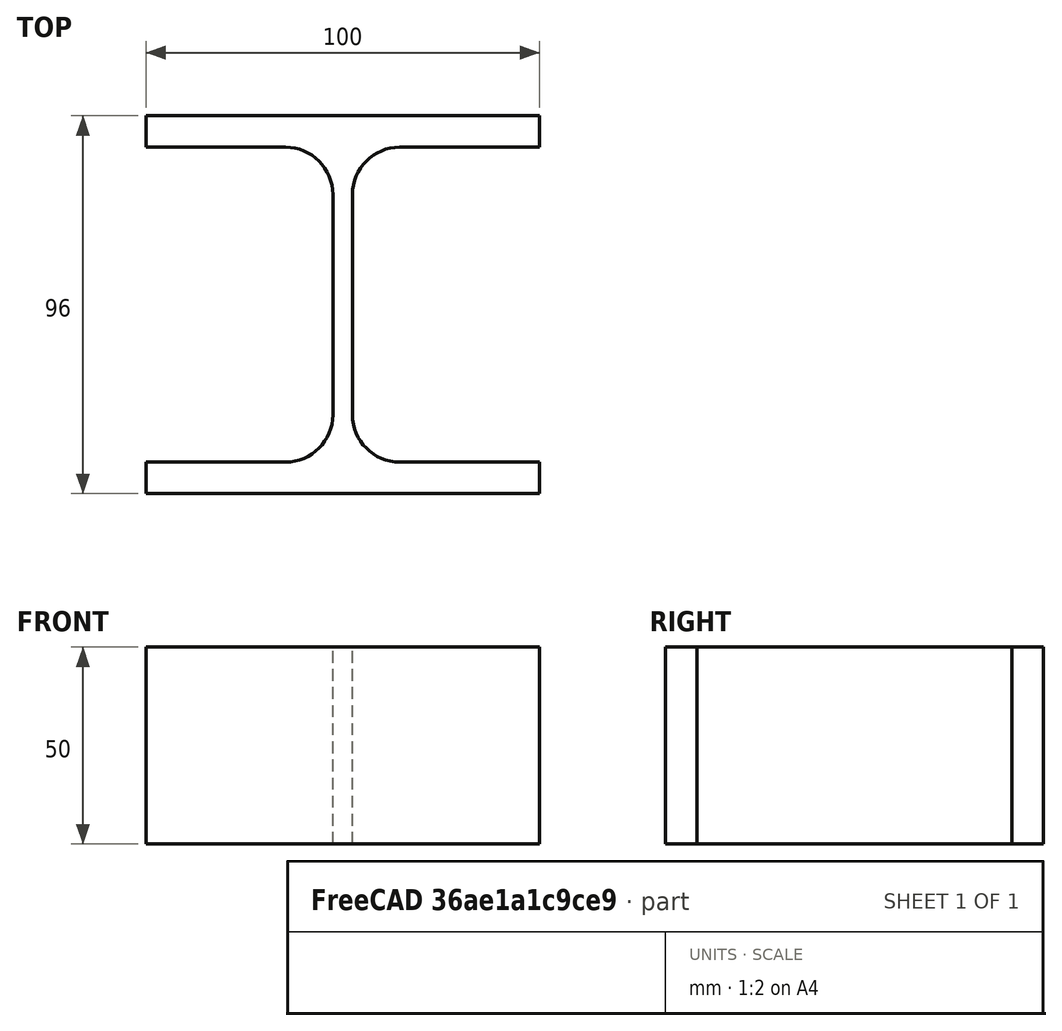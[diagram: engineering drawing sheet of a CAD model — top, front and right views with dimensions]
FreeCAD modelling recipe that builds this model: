
FCSTD DOCUMENT  (FreeCAD 0.15R4671 (Git))
Label: HE-A-Profile 100 DIN1025-3 S235JR
License: All rights reserved
LicenseURL: http://en.wikipedia.org/wiki/All_rights_reserved
objects: Sketcher::SketchObject×1, Part::Extrusion×1
note: 2 computed .brp shape members not serialized (recipe doc carries the construction recipe); baked Part::Feature solids carry a one-line shape summary decoded from their .brp

FEATURE [Sketcher::SketchObject] Sketch
  sketch-geometry (16):
    g0: LineSegment StartX=2.5 StartY=-28 StartZ=0 EndX=2.5 EndY=28 EndZ=0
    g1: LineSegment StartX=14.5 StartY=40 StartZ=0 EndX=50 EndY=40 EndZ=0
    g2: LineSegment StartX=50 StartY=40 StartZ=0 EndX=50 EndY=48 EndZ=0
    g3: LineSegment StartX=50 StartY=48 StartZ=0 EndX=-50 EndY=48 EndZ=0
    g4: LineSegment StartX=-50 StartY=48 StartZ=0 EndX=-50 EndY=40 EndZ=0
    g5: LineSegment StartX=-50 StartY=40 StartZ=0 EndX=-14.5 EndY=40 EndZ=0
    g6: LineSegment StartX=-2.5 StartY=28 StartZ=0 EndX=-2.5 EndY=-28 EndZ=0
    g7: LineSegment StartX=-14.5 StartY=-40 StartZ=0 EndX=-50 EndY=-40 EndZ=0
    g8: LineSegment StartX=-50 StartY=-40 StartZ=0 EndX=-50 EndY=-48 EndZ=0
    g9: LineSegment StartX=-50 StartY=-48 StartZ=0 EndX=50 EndY=-48 EndZ=0
    g10: LineSegment StartX=50 StartY=-48 StartZ=0 EndX=50 EndY=-40 EndZ=0
    g11: LineSegment StartX=50 StartY=-40 StartZ=0 EndX=14.5 EndY=-40 EndZ=0
    g12: ArcOfCircle CenterX=14.5 CenterY=28 CenterZ=0 NormalX=0 NormalY=0 NormalZ=1 Radius=12 StartAngle=1.5708 EndAngle=3.14159
    g13: ArcOfCircle CenterX=14.5 CenterY=-28 CenterZ=0 NormalX=0 NormalY=0 NormalZ=1 Radius=12 StartAngle=3.14159 EndAngle=4.71239
    g14: ArcOfCircle CenterX=-14.5 CenterY=28 CenterZ=0 NormalX=0 NormalY=0 NormalZ=1 Radius=12 StartAngle=0 EndAngle=1.5708
    g15: ArcOfCircle CenterX=-14.5 CenterY=-28 CenterZ=0 NormalX=0 NormalY=0 NormalZ=1 Radius=12 StartAngle=4.71239 EndAngle=6.28319
  constraints (42):
    c: Vertical(g0)
    c: Coincident(g2,g1)
    c: Vertical(g2)
    c: Coincident(g3,g2)
    c: Coincident(g4,g3)
    c: Vertical(g4)
    c: Coincident(g5,g4)
    c: Horizontal(g5)
    c: Vertical(g6)
    c: Horizontal(g7)
    c: Coincident(g8,g7)
    c: Vertical(g8)
    c: Coincident(g9,g8)
    c: Horizontal(g9)
    c: Coincident(g10,g9)
    c: Vertical(g10)
    c: Coincident(g11,g10)
    c: Horizontal(g11)
    c: Tangent(g1,g12) = 1.5708
    c: Tangent(g0,g12) = 1.5708
    c: Tangent(g0,g13) = 1.5708
    c: Tangent(g11,g13) = 1.5708
    c: Tangent(g5,g14) = 1.5708
    c: Tangent(g6,g14) = 1.5708
    c: Tangent(g6,g15) = 1.5708
    c: Tangent(g7,g15) = 1.5708
    c: Equal(g3,g9)
    c: Equal(g2,g4)
    c: Equal(g4,g8)
    c: Equal(g8,g10)
    c: Equal(g12,g14)
    c: Equal(g14,g15)
    c: Equal(g15,g13)
    c: Symmetric(g2,g3,g-2)
    c: Symmetric(g9,g8,g-2)
    c: Symmetric(g0,g6,g-2)
    c: Symmetric(g2,g9,g-1)
    c: DistanceY(g2,g9) = -96
    c: DistanceX(g3) = -100
    c: DistanceX(g0,g6) = -5
    c: DistanceY(g2) = 8
    c: Radius(g12) = 12
FEATURE [Part::Extrusion] Extrude  label="HE-A-Profile 100 DIN1025-3 S235JR"
  Base = -> Sketch
  Dir = (0,0,50)
  Solid = true
